# Revit family: Access_Door-Acudor-Recessed-AP-5010_Series
name_source: partatom
category: Specialty Equipment
revit_build: Autodesk Revit 2014 (Build: 20130308_1515(x64)
units: mm (PartAtom-declared; Revit-internal decimal feet)

## types (4) — shared parameters
Allen Head Cam Latch = No
Assembly Code = C1020700
CL - Cylinder Lock (one per door) = No
Ceiling Mounted = No
Default Elevation = 48"
Description = Recessed Access Door for Acoustal Plaster Walls and Ceilings
Finish = Steel-Acudor-White Alkyd Enamel
Installation Type = Wall Mounted
Length = 2"
Manufacturer = Acudor
Material = Steel-Acudor-White Alkyd Enamel
Mortise Cylinder Lock (Prepare for/or Installed) = No
Product Documentation Link = https://www.acudor.com
Product Page URL = https://www.acudor.com
SC - stainless steel screwdriver operated cam latch = No
Spanner Head Cam Latch = No
Torx Cam Latch = No
URL = http://acudor.com
Wall Mounted = Yes

## per-type parameters (varying)
| type | 1 Latch | 2 Latches | 4 Latches | Height | Width |
| AP-5010 12x12 | Yes | No | No | 12" | 12" |
| AP-5010 18x18 | No | Yes | No | 18" | 18" |
| AP-5010 24x24 | No | Yes | No | 24" | 24" |
| AP-5010 24x36 | No | Yes | Yes | 36" | 24" |

note: column(s) folded — value = type name in every type: Model

## geometry (parser evidence)
native form markers: Sweep x1
no freeform markers — native parametric forms only
